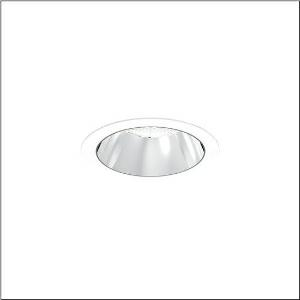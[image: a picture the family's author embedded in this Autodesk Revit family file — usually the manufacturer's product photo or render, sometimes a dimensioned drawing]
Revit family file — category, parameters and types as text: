
# Revit family: lunis_21_l_51db15td91c
name_source: partatom
category: Lighting Fixtures
units: mm (PartAtom-declared; Revit-internal decimal feet)

## family parameters
Cut with Voids When Loaded = No
Host = Face
Light Source = No
Part Type = Normal
Room Calculation Point = No
Round Connector Dimension = Use Diameter
Shared = No

## types (1)
- --- (1 x LED 3000 K ... 6500 K, 4100 lm, 25.4 W, 4000K)
    Apparent Load = 25 VA
    CIE Flux Codes = 93 100 100 100 100
    Color Rendering = 80
    Color Temperature = 4000K
    Default Elevation = 1800 mm
    Description = Lunis 21 L, downlight, light control with lens, of PMMA, anti glare with reflector, of aluminium, highly specular, light emission: direct distribution, LED rated luminous flux: 4.100lm, light colour: 8tw, with terminal, 5-pole, mains connection: 220..240V, AC/DC, 0/50..60Hz, housing, round, of diecast aluminium, traffic white (RAL 9016), diameter: 165mm, clamping range: 1..40mm, protection rating (complete): IP20, protection rating (on room side): IP54, insulation class (complete): insulation class II (safety insulation), certification: CE, impact resistance: IK03, packaging unit: 1 piece
    Height = 0 mm  [stored 0 ft]
    Lamp = 1 x LED 3000 K ... 6500 K
    Lamp Light Flux = 4100 lm
    Lamp Power = 25.4 W
    Lamp count = 1
    Length = 165 mm
    Luminous efficacy = 161 lm/W
    Manufacturer = Siteco
    ModVariant = No
    Model = 51DB15TD91C
    Mounting Place = Ceiling
    Mounting Type = Recessed
    Number of Poles = 1
    OnlyDefault = Yes
    Power Factor = 1
    Product Name = Lunis 21 L
    Product group = downlight
    ProductGroupID = 401
    Protection Class = Protection class II
    Protection Degree = IP 20
    RLX_Detail_Level = 1
    RLX_Emergency_Light_Flux = 0 lm
    RLX_Emergency_Type = 0
    RLX_Emergency_Type_DB = No
    RlxData = <blob elided: 14817 chars, md5=58ff4058>
    Socket = socket
    Standby Power = 0 W
    System Light Flux = 4100 lm
    System Power = 25 W
    Type Comments = individual setting: CCT=4000K, colour temperature 4000K, luminous flux: 100 % | (ON | ON | OFF | OFF) | 700 mA
    Type Image = l_1291167.jpg
    URL = http://relux.com
    VarID = @adj_036247
    Voltage = 0 V
    Weight = 0.00 kg
    Width = 0 mm  [stored 0 ft]

note: [stored X ft] marks values corroborated as IEEE doubles in the binary element streams (Revit-internal decimal feet)

## geometry (parser evidence)
native form markers: Sweep x12
no freeform markers — native parametric forms only
